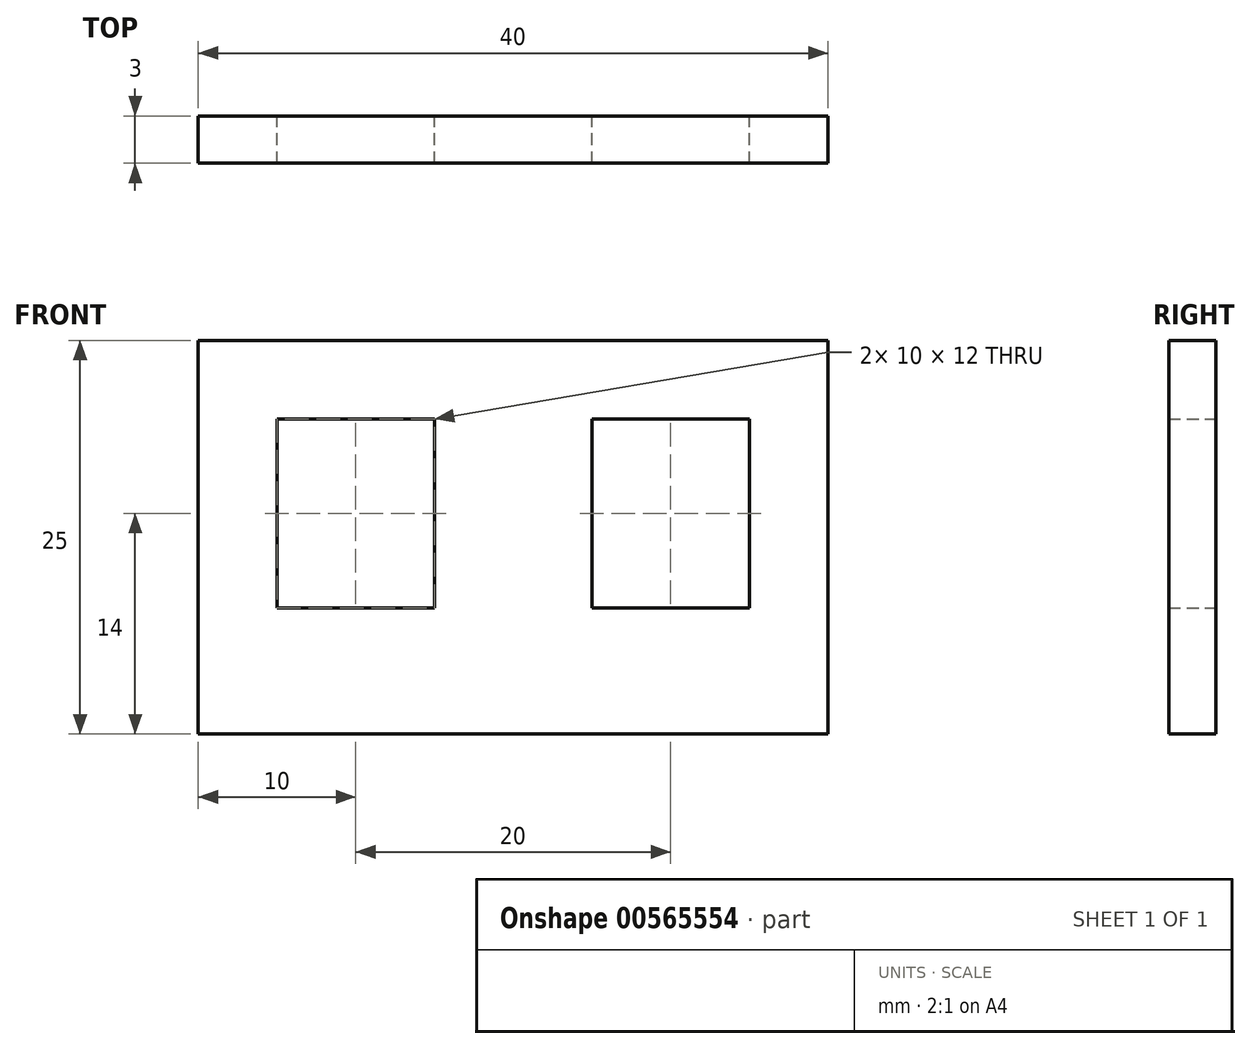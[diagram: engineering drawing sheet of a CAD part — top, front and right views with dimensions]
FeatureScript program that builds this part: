
annotation { "Feature Type Name" : "Feature", "Feature Type Description" : "" }
export const myFeature = defineFeature(function(context is Context, id is Id, definition is map)
    precondition{}
    {
        {
            var Q0;
            Q0=qCreatedBy(makeId("Front.planeOp"),FACE);
            var sketch = newSketch(context, id + "F0", { "sketchPlane" : qUnion([Q0])});
            skLineSegment(sketch, "E0.bottom", {"start": v(20, -12.5) * mm, "end": v(-20, -12.5) * mm});
            skLineSegment(sketch, "E0.top", {"start": v(20, 12.5) * mm, "end": v(-20, 12.5) * mm});
            skLineSegment(sketch, "E0.left", {"start": v(20, -12.5) * mm, "end": v(20, 12.5) * mm});
            skLineSegment(sketch, "E0.right", {"start": v(-20, -12.5) * mm, "end": v(-20, 12.5) * mm});
            skPoint(sketch, "E0.middle", {"position": v(0, 0) * mm});
            skLineSegment(sketch, "E1.bottom", {"start": v(-5, -4.5) * mm, "end": v(-15, -4.5) * mm});
            skLineSegment(sketch, "E1.top", {"start": v(-5, 7.5) * mm, "end": v(-15, 7.5) * mm});
            skLineSegment(sketch, "E1.left", {"start": v(-5, -4.5) * mm, "end": v(-5, 7.5) * mm});
            skLineSegment(sketch, "E1.right", {"start": v(-15, -4.5) * mm, "end": v(-15, 7.5) * mm});
            skPoint(sketch, "E1.middle", {"position": v(-10, 1.5) * mm});
            skLineSegment(sketch, "E2.bottom", {"start": v(15, -4.5) * mm, "end": v(5, -4.5) * mm});
            skLineSegment(sketch, "E2.top", {"start": v(15, 7.5) * mm, "end": v(5, 7.5) * mm});
            skLineSegment(sketch, "E2.left", {"start": v(15, -4.5) * mm, "end": v(15, 7.5) * mm});
            skLineSegment(sketch, "E2.right", {"start": v(5, -4.5) * mm, "end": v(5, 7.5) * mm});
            skPoint(sketch, "E2.middle", {"position": v(10, 1.5) * mm});
            skSolve(sketch);
        }
        {
            var Q0;
            Q0 = qSketchRegion(id + "F0", true);
            extrude(context, id + "F1", {"entities" : qUnion([Q0]), "depth" : 3 * mm, "offsetDistance" : 25 * mm});
        }
    });
